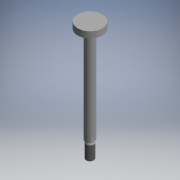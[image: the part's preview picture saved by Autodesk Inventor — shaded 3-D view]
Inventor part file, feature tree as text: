
AUTODESK INVENTOR PART (.ipt)
format: ipt  version: 2017.3 (Build 213256000, 256)  size: 137,728 bytes
history: native  units: mm (DEFAULTED — no unit token found)
features: other x28, sketch x3, revolve x2, thread x1, extrude x1
ambient origin geometry x8: Origin, YZ Plane, XZ Plane, XY Plane, X Axis, Y Axis, Z Axis, Center Point
bodies: Solid1 (feature_tree)
feature tree (35):
  revolve  "Revolution1"  Angle=360.0deg
  revolve  "Revolution2"  [1 undecoded]
  thread  "Thread1"  [1 undecoded]
  extrude  "Extrusion1"  [1 undecoded]
  other  "FDT_KSAUFSATZ_XY"
  other  "FDT_KSAUFSATZ_YZ"
  other  "FDT_KSAUFSATZ_ZX"
  other  "FDT_KSAUFSATZ_X"
  other  "FDT_KSAUFSATZ_Y"
  other  "FDT_KSAUFSATZ_Z"
  other  "FDT_KSAUFSATZ_Center"
  other  "FDT_NUT_XY"
  other  "FDT_NUT_YZ"
  other  "FDT_NUT_ZX"
  other  "FDT_NUT_X"
  other  "FDT_NUT_Y"
  other  "FDT_NUT_Z"
  other  "FDT_NUT_Center"
  other  "KS_XY"
  other  "KS_YZ"
  other  "KS_ZX"
  other  "KS_X"
  other  "KS_Y"
  other  "KS_Z"
  other  "KS_Center"
  other  "NUT1_XY"
  other  "NUT1_YZ"
  other  "NUT1_ZX"
  other  "NUT1_X"
  other  "NUT1_Y"
  other  "NUT1_Z"
  other  "NUT1_Center"
  sketch  "Sketch_2"  dims[d0=360.0deg d1=360.0deg]
  sketch  "Sketch_6"  dims[d2=17.535mm d3=0.0mm d4=7.0mm d5=0.0mm]
  sketch  "Sketch_7"
note: 3 required parameter values undecoded (feature->parameter linkage not recoverable at this tier; creation-order binding heuristic only, values carry confidence <= 0.55)